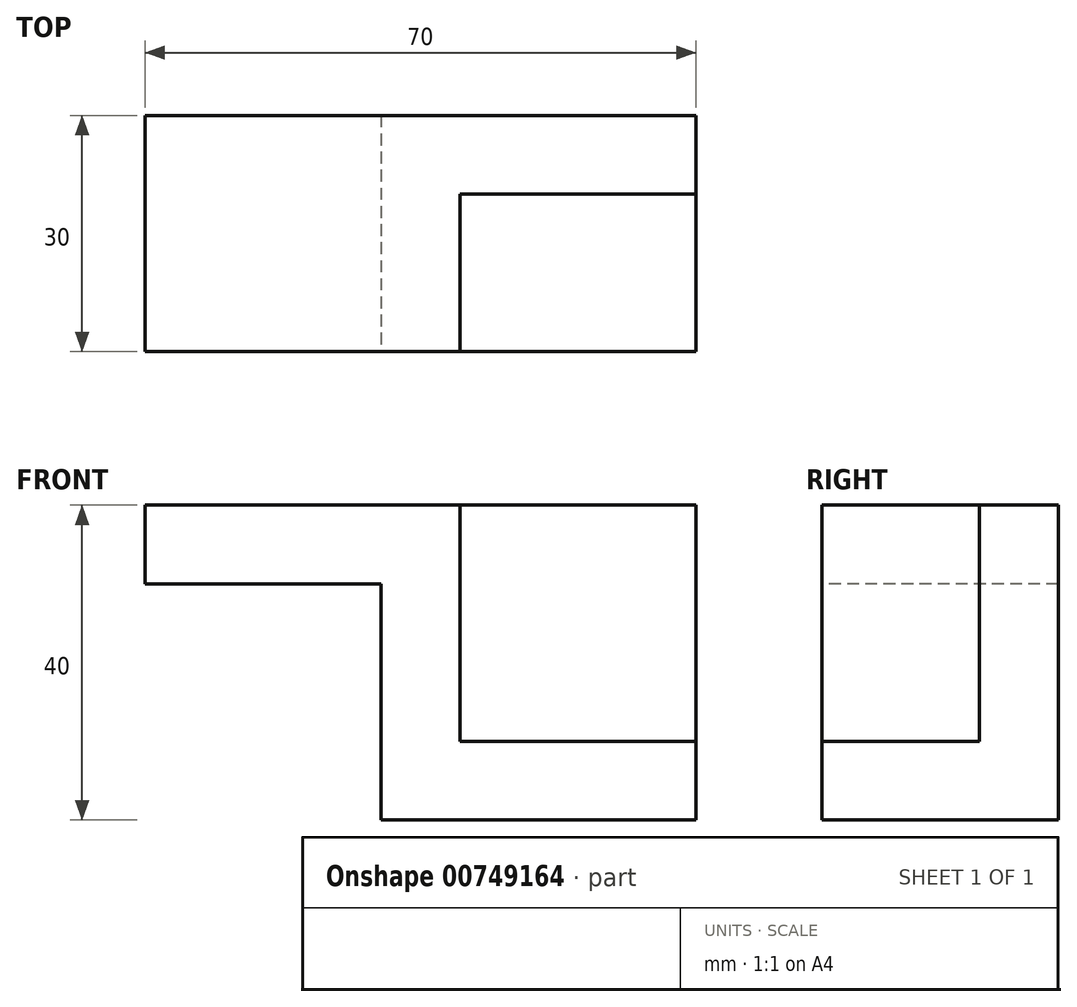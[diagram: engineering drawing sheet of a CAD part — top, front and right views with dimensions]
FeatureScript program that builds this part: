
annotation { "Feature Type Name" : "Feature", "Feature Type Description" : "" }
export const myFeature = defineFeature(function(context is Context, id is Id, definition is map)
    precondition{}
    {
        {
            var Q0;
            Q0=qCreatedBy(makeId("Top.planeOp"),FACE);
            var sketch = newSketch(context, id + "F0", { "sketchPlane" : qUnion([Q0])});
            skLineSegment(sketch, "E0", {"start": v(0, 0) * mm, "end": v(30, 0) * mm});
            skLineSegment(sketch, "E1", {"start": v(30, 0) * mm, "end": v(30, 20) * mm});
            skLineSegment(sketch, "E2", {"start": v(30, 20) * mm, "end": v(0, 20) * mm});
            skLineSegment(sketch, "E3", {"start": v(0, 20) * mm, "end": v(0, 0) * mm});
            skLineSegment(sketch, "E4", {"start": v(30, 30) * mm, "end": v(-10, 30) * mm});
            skLineSegment(sketch, "E5", {"start": v(-10, 30) * mm, "end": v(-10, 0) * mm});
            skLineSegment(sketch, "E6", {"start": v(30, 30) * mm, "end": v(30, 20) * mm});
            skLineSegment(sketch, "E7", {"start": v(0, 0) * mm, "end": v(-10, 0) * mm});
            skSolve(sketch);
        }
        {
            var Q0;
            Q0=makeQuery(id+"F0.imprint","IMPRINT",FACE,{"disambiguationData":[TD([[makeQuery(id+"F0.imprint","IMPRINT",EDGE,{"derivedFrom":sQuery(id+"F0.wireOp",EDGE,"E0")}),1.0]])]});
            extrude(context, id + "F1", {"entities" : qUnion([Q0]), "depth" : 10 * mm, "offsetDistance" : 25 * mm});
        }
        {
            var Q0;
            Q0=makeQuery(id+"F0.imprint","IMPRINT",FACE,{"disambiguationData":[TD([[makeQuery(id+"F0.imprint","IMPRINT",EDGE,{"derivedFrom":sQuery(id+"F0.wireOp",EDGE,"E2")}),-1.0]])]});
            extrude(context, id + "F2", {"entities" : qUnion([Q0]), "operationType" : NewBodyOperationType.ADD, "depth" : 40 * mm, "offsetDistance" : 25 * mm});
        }
        {
            var Q0;
            Q0=makeQuery(id+"F2.opExtrude","SWEPT_FACE",FACE,{"disambiguationData":[OSD([sQuery(id+"F0.wireOp",EDGE,"E5")])]});
            var sketch = newSketch(context, id + "F3", { "sketchPlane" : qUnion([Q0])});
            skLineSegment(sketch, "E8", {"start": v(-30, 40) * mm, "end": v(-30, 30) * mm});
            skLineSegment(sketch, "E9", {"start": v(-30, 30) * mm, "end": v(0, 30) * mm});
            skLineSegment(sketch, "E10", {"start": v(0, 30) * mm, "end": v(0, 40) * mm});
            skSolve(sketch);
        }
        {
            var Q0;
            Q0=makeQuery(id+"F3.imprint","IMPRINT",FACE,{"disambiguationData":[TD([[makeQuery(id+"F3.imprint","IMPRINT",EDGE,{"derivedFrom":sQuery(id+"F3.wireOp",EDGE,"E8")}),1.0]])]});
            extrude(context, id + "F4", {"entities" : qUnion([Q0]), "operationType" : NewBodyOperationType.ADD, "depth" : 30 * mm, "offsetDistance" : 25 * mm});
        }
    });
